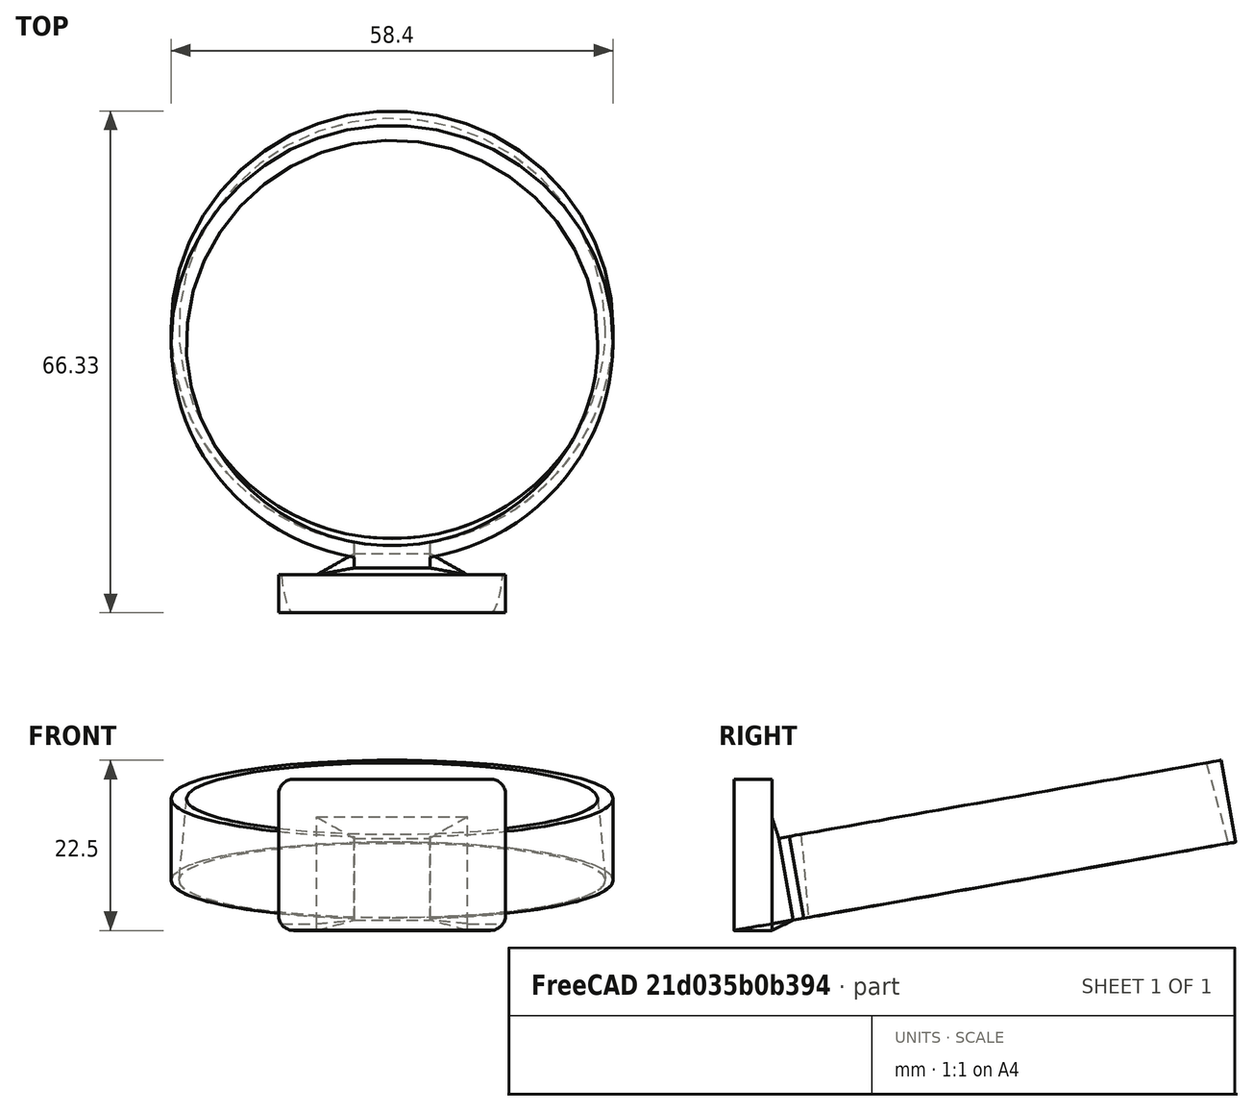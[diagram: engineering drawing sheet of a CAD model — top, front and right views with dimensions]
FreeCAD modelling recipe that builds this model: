
FCSTD DOCUMENT  (FreeCAD 0.21R33771 (Git))
Label: clock_holder
License: All rights reserved
LicenseURL: http://en.wikipedia.org/wiki/All_rights_reserved
objects: Part::FeaturePython×5, Part::Box×3, Part::MultiFuse×2, Part::Cone×1, Part::Cylinder×1, Part::Cut×1, Part::Fillet×1, Part::Compound×1, Part::Loft×1, Part::Plane×1, App::DocumentObjectGroup×1
note: 17 computed .brp shape members not serialized (recipe doc carries the construction recipe); baked Part::Feature solids carry a one-line shape summary decoded from their .brp

FEATURE [Part::Cone] Cone
  Angle = 360
  AttacherType = Attacher::AttachEngine3D
  Height = 11
  Radius1 = 28.2
  Radius2 = 27.2
  expr: Radius1 = Radius2 + 1 mm
FEATURE [Part::Cylinder] Cylinder
  Angle = 360
  AttacherType = Attacher::AttachEngine3D
  FirstAngle = 0
  Height = 11
  Radius = 29.2
  SecondAngle = 0
  expr: Height = Cone.Height
  expr: Radius = Cone.Radius1 + 1 mm
FEATURE [Part::Cut] Cut
  Base = -> Cylinder
  Tool = -> Cone
FEATURE [Part::Box] Box  label="Cube"
  AttacherType = Attacher::AttachEngine3D
  Height = 20
  Length = 30
  Placement = pos=(-15,-33.2,0) rot=(0,0,1;0rad)
  Width = 5
  expr: .Placement.Base.x = -Length / 2
  expr: .Placement.Base.y = -Cone.Radius1 - Width
FEATURE [Part::Box] Box001  label="Cube001"
  AttacherType = Attacher::AttachEngine3D
  Height = 11
  Length = 10
  Placement = pos=(-5,-30.2,0) rot=(0,0,1;0rad)
  Width = 2
  expr: .Placement.Base.x = -Length / 2
  expr: .Placement.Base.y = -Cone.Radius1 - Width
  expr: Height = Cone.Height
FEATURE [Part::MultiFuse] Fusion
  Placement = pos=(0,4.37129,6.40125) rot=(-1,0,0;6.10865rad)
  Shapes = -> [Cut,Box001]
FEATURE [Part::Box] Box002  label="Cube002"
  AttacherType = Attacher::AttachEngine3D
  Height = 15
  Length = 20
  Placement = pos=(-10,-33.2,0) rot=(0,0,1;0rad)
  Width = 5
  expr: .Placement.Base.x = -Length / 2
  expr: .Placement.Base.y = -Cone.Radius1 - Width
  expr: Width = <<Cube>>.Width
FEATURE [Part::Fillet] Fillet
  Base = -> Box
  Edges = 4 edges r=2: [Edge2,Edge4,Edge6,Edge8]
FEATURE [Part::Compound] Compound
  Links = -> [Fusion]
  Placement = pos=(0,0,0.2) rot=(0,0,1;0rad)
FEATURE [Part::FeaturePython] Facebinder  # WARN: FeaturePython — macro-defined, semantics opaque (R4)
  Area = 110
  Extrusion = 0
  Faces = -> [Compound]
  RemoveSplitter = false
  Sew = false
FEATURE [Part::FeaturePython] Facebinder001  # WARN: FeaturePython — macro-defined, semantics opaque (R4)
  Area = 300
  Extrusion = 0
  Faces = -> [Box002]
  RemoveSplitter = false
  Sew = false
FEATURE [Part::Loft] Loft
  Closed = false
  MaxDegree = 5
  Ruled = false
  Sections = -> [Facebinder001,Facebinder]
  Solid = true
FEATURE [Part::MultiFuse] Fusion001
  Shapes = -> [Box002,Fillet,Compound,Loft]
FEATURE [Part::Plane] Plane
  AttacherType = Attacher::AttachEngine3D
  Length = 100
  Placement = pos=(-46.5,-41.5527,-1.46962) rot=(1,0,0;0.174533rad)
  Width = 100
FEATURE [Part::FeaturePython] Slice  # WARN: FeaturePython — macro-defined, semantics opaque (R4)
  Base = -> Fusion001
  Mode = 1
  Tolerance = 0
  Tools = -> [Plane]
FEATURE [Part::FeaturePython] Slice_child0  label="Slice.0"  # WARN: FeaturePython — macro-defined, semantics opaque (R4)
  Base = -> Slice
  FilterType = 1
  Invert = false
  OverrideMaxVal = 0
  WindowFrom = 80
  WindowTo = 100
  items = 0
FEATURE [Part::FeaturePython] Slice_child1  label="clock holder"  # WARN: FeaturePython — macro-defined, semantics opaque (R4)
  Base = -> Slice
  FilterType = 1
  Invert = false
  OverrideMaxVal = 0
  WindowFrom = 80
  WindowTo = 100
  items = 1
FEATURE [App::DocumentObjectGroup] GrExplode_Slice  label="Exploded Slice"
  Group = -> [Slice_child0,Slice_child1]
